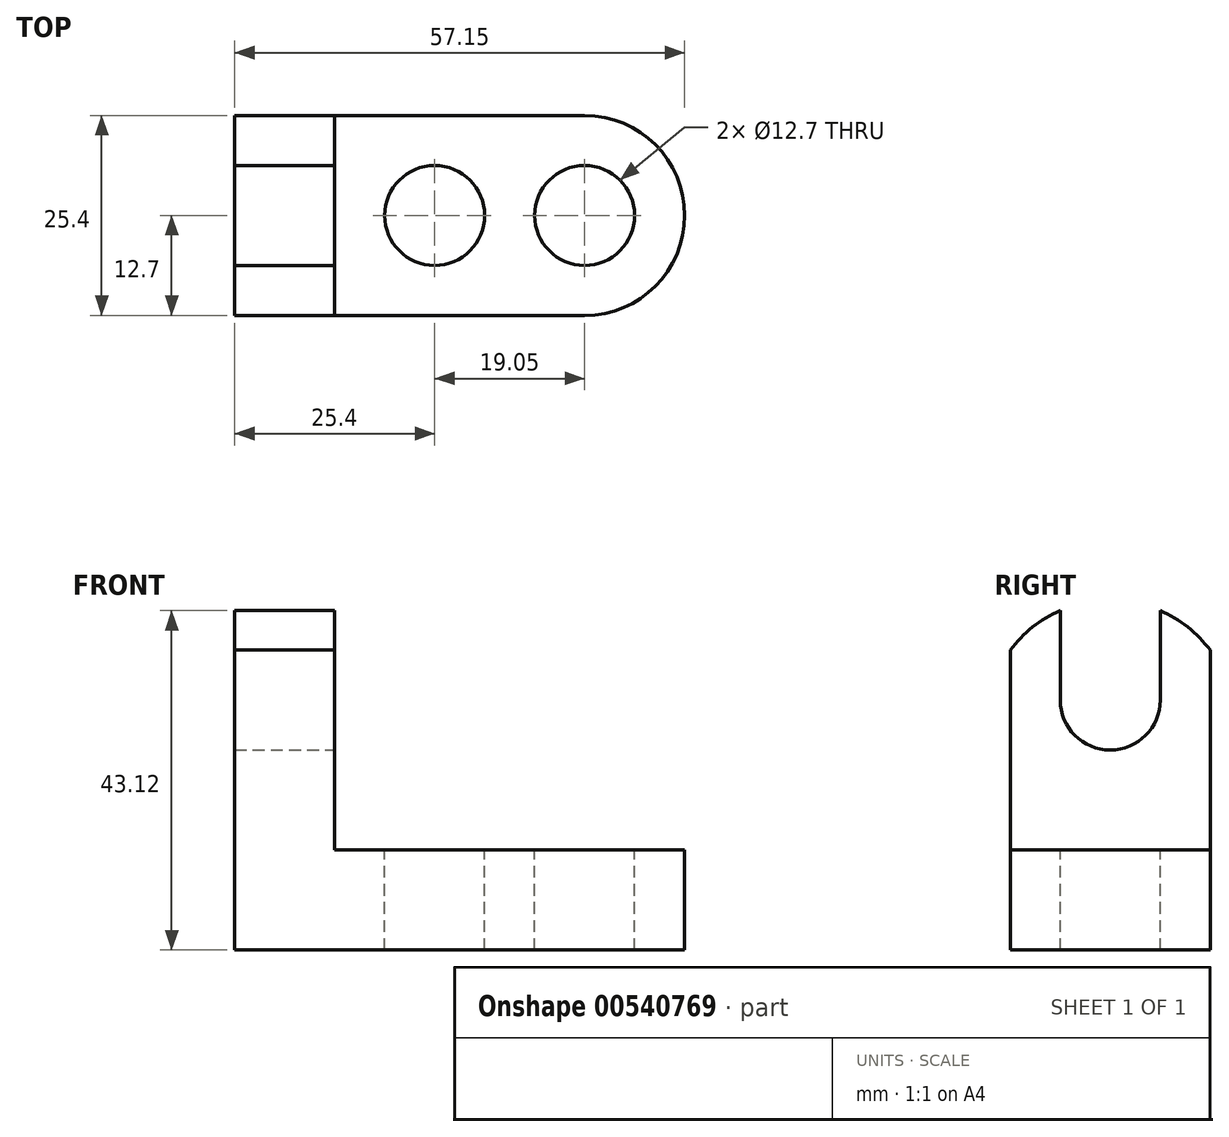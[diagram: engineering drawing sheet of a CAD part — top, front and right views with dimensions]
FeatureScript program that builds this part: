
annotation { "Feature Type Name" : "Feature", "Feature Type Description" : "" }
export const myFeature = defineFeature(function(context is Context, id is Id, definition is map)
    precondition{}
    {
        {
            var Q0;
            Q0=qCreatedBy(makeId("Front.planeOp"),FACE);
            var sketch = newSketch(context, id + "F0", { "sketchPlane" : qUnion([Q0])});
            skLineSegment(sketch, "E0", {"start": v(0, 0) * mm, "end": v(57.15, 0) * mm});
            skLineSegment(sketch, "E1", {"start": v(57.15, 0) * mm, "end": v(57.15, 12.7) * mm});
            skLineSegment(sketch, "E2", {"start": v(57.15, 12.7) * mm, "end": v(12.7, 12.7) * mm});
            skLineSegment(sketch, "E3", {"start": v(12.7, 12.7) * mm, "end": v(12.7, 44.45) * mm});
            skLineSegment(sketch, "E4", {"start": v(12.7, 44.45) * mm, "end": v(0, 44.45) * mm});
            skLineSegment(sketch, "E5", {"start": v(0, 44.45) * mm, "end": v(0, 0) * mm});
            skSolve(sketch);
        }
        {
            var Q0;
            Q0 = qSketchRegion(id + "F0", true);
            extrude(context, id + "F1", {"entities" : qUnion([Q0]), "depth" : 25.4 * mm, "offsetDistance" : 25.4 * mm});
        }
        {
            var Q0;
            Q0=makeQuery(id+"F1.opExtrude","SWEPT_FACE",FACE,{"disambiguationData":[OSD([sQuery(id+"F0.wireOp",EDGE,"E2")])]});
            var sketch = newSketch(context, id + "F2", { "sketchPlane" : qUnion([Q0])});
            skCircle(sketch, "E6", {"center": v(25.4, -12.7) * mm, "radius": 6.35 * mm});
            skCircle(sketch, "E7", {"center": v(44.45, -12.7) * mm, "radius": 6.35 * mm});
            skSolve(sketch);
        }
        {
            var Q0;
            Q0=makeQuery(id+"F2.imprint","IMPRINT",FACE,{"disambiguationData":[TD([[makeQuery(id+"F2.imprint","IMPRINT",EDGE,{"derivedFrom":sQuery(id+"F2.wireOp",EDGE,"E6")}),1.0]])]});
            var Q1;
            Q1=makeQuery(id+"F2.imprint","IMPRINT",FACE,{"disambiguationData":[TD([[makeQuery(id+"F2.imprint","IMPRINT",EDGE,{"derivedFrom":sQuery(id+"F2.wireOp",EDGE,"E7")}),1.0]])]});
            extrude(context, id + "F3", {"entities" : qUnion([Q0, Q1]), "operationType" : NewBodyOperationType.REMOVE, "oppositeDirection" : true, "depth" : 12.7 * mm, "offsetDistance" : 25.4 * mm});
        }
        {
            var Q0;
            Q0=makeQuery(id+"F1.opExtrude","SWEPT_FACE",FACE,{"disambiguationData":[OSD([sQuery(id+"F0.wireOp",EDGE,"E3")])]});
            var sketch = newSketch(context, id + "F4", { "sketchPlane" : qUnion([Q0])});
            skSolve(sketch);
        }
        {
            var Q0;
            Q0=makeQuery(id+"F1.opExtrude","SWEPT_FACE",FACE,{"disambiguationData":[OSD([sQuery(id+"F0.wireOp",EDGE,"E2")])]});
            var sketch = newSketch(context, id + "F5", { "sketchPlane" : qUnion([Q0])});
            skArc(sketch, "E8", {"start": v(44.45, -25.4) * mm, "mid": v(57.15, -12.7) * mm, "end": v(44.45, 0) * mm});
            skSolve(sketch);
        }
        {
            var Q0;
            {var subQ0=sQuery(id+"F5.wireOp",EDGE,"E8");var subQ1=sQuery(id+"F0.wireOp",EDGE,"E2");var subQ2=makeQuery(id+"F1.opExtrude","CAP_EDGE",EDGE,{"disambiguationData":[OSD([subQ1])],"isStart":true});var subQ3=makeQuery(id+"F5.imprint","INTERSECT",VERTEX,{"derivedFrom":[subQ2,subQ0]});Q0=makeQuery(id+"F5.imprint","IMPRINT",FACE,{"disambiguationData":[TD([[makeQuery(id+"F5.imprint","IMPRINT",EDGE,{"disambiguationData":[TD([[subQ3,1.0]])],"derivedFrom":subQ0}),-1.0]])]});}
            var Q1;
            {var subQ0=sQuery(id+"F5.wireOp",EDGE,"E8");var subQ1=sQuery(id+"F0.wireOp",EDGE,"E2");var subQ2=makeQuery(id+"F1.opExtrude","CAP_EDGE",EDGE,{"disambiguationData":[OSD([subQ1])],"isStart":false});var subQ3=makeQuery(id+"F5.imprint","INTERSECT",VERTEX,{"derivedFrom":[subQ2,subQ0]});Q1=makeQuery(id+"F5.imprint","IMPRINT",FACE,{"disambiguationData":[TD([[makeQuery(id+"F5.imprint","IMPRINT",EDGE,{"disambiguationData":[TD([[subQ3,-1.0]])],"derivedFrom":subQ0}),-1.0]])]});}
            extrude(context, id + "F6", {"entities" : qUnion([Q0, Q1]), "operationType" : NewBodyOperationType.REMOVE, "oppositeDirection" : true, "depth" : 12.7 * mm, "offsetDistance" : 25.4 * mm});
        }
        {
            var Q0;
            {var subQ0=sQuery(id+"F0.wireOp",EDGE,"E3");Q0=makeQuery(id+"F4.imprint","IMPRINT",FACE,{"disambiguationData":[TD([[makeQuery(id+"F4.imprint","IMPRINT",EDGE,{"derivedFrom":makeQuery(id+"F1.opExtrude","CAP_EDGE",EDGE,{"disambiguationData":[OSD([subQ0])],"isStart":true})}),1.0]])]});}
            var sketch = newSketch(context, id + "F7", { "sketchPlane" : qUnion([Q0])});
            skLineSegment(sketch, "E9.0", {"start": v(-25.4, 44.45) * mm, "end": v(0, 44.45) * mm});
            skCircle(sketch, "E10", {"center": v(-12.7, 31.75) * mm, "radius": 6.35 * mm});
            skLineSegment(sketch, "E11", {"start": v(-19.05, 31.75) * mm, "end": v(-19.05, 44.45) * mm});
            skLineSegment(sketch, "E12", {"start": v(-6.35, 31.75) * mm, "end": v(-6.35, 44.45) * mm});
            skSolve(sketch);
        }
        {
            var Q0;
            {var subQ0=sQuery(id+"F7.wireOp",EDGE,"E10");var subQ1=makeQuery(id+"F7.imprint","INTERSECT",VERTEX,{"derivedFrom":[subQ0,sQuery(id+"F7.wireOp",EDGE,"E11")]});Q0=makeQuery(id+"F7.imprint","IMPRINT",FACE,{"disambiguationData":[TD([[makeQuery(id+"F7.imprint","IMPRINT",EDGE,{"disambiguationData":[TD([[subQ1,1.0]])],"derivedFrom":subQ0}),1.0]])]});}
            var Q1;
            {var subQ0=sQuery(id+"F7.wireOp",EDGE,"E11");Q1=makeQuery(id+"F7.imprint","IMPRINT",FACE,{"disambiguationData":[TD([[makeQuery(id+"F7.imprint","IMPRINT",EDGE,{"derivedFrom":subQ0}),-1.0]])]});}
            extrude(context, id + "F8", {"entities" : qUnion([Q0, Q1]), "operationType" : NewBodyOperationType.REMOVE, "oppositeDirection" : true, "depth" : 12.7 * mm, "offsetDistance" : 25.4 * mm});
        }
        {
            var Q0;
            {var subQ0=sQuery(id+"F0.wireOp",EDGE,"E3");Q0=makeQuery(id+"F4.imprint","IMPRINT",FACE,{"disambiguationData":[TD([[makeQuery(id+"F4.imprint","IMPRINT",EDGE,{"derivedFrom":makeQuery(id+"F1.opExtrude","CAP_EDGE",EDGE,{"disambiguationData":[OSD([subQ0])],"isStart":true})}),1.0]])]});}
            var sketch = newSketch(context, id + "F9", { "sketchPlane" : qUnion([Q0])});
            skLineSegment(sketch, "E13.0", {"start": v(-25.4, 12.7) * mm, "end": v(-25.4, 44.45) * mm});
            skLineSegment(sketch, "E13.1", {"start": v(0, 44.45) * mm, "end": v(0, 0) * mm});
            skArc(sketch, "E14", {"start": v(0, 38.1) * mm, "mid": v(-12.7, 44.45) * mm, "end": v(-25.4, 38.1) * mm});
            skSolve(sketch);
        }
        {
            var Q0;
            {var subQ0=sQuery(id+"F9.wireOp",EDGE,"E13.0");var subQ3=sQuery(id+"F9.wireOp",EDGE,"E14");var subQ4=makeQuery(id+"F9.imprint","INTERSECT",VERTEX,{"derivedFrom":[subQ0,subQ3]});Q0=makeQuery(id+"F9.imprint","IMPRINT",FACE,{"disambiguationData":[TD([[makeQuery(id+"F9.imprint","IMPRINT",EDGE,{"disambiguationData":[TD([[subQ4,-1.0]])],"derivedFrom":subQ0}),-1.0]])]});}
            var Q1;
            {var subQ0=sQuery(id+"F9.wireOp",EDGE,"E13.1");var subQ3=sQuery(id+"F9.wireOp",EDGE,"E14");var subQ4=makeQuery(id+"F9.imprint","INTERSECT",VERTEX,{"derivedFrom":[subQ0,subQ3]});Q1=makeQuery(id+"F9.imprint","IMPRINT",FACE,{"disambiguationData":[TD([[makeQuery(id+"F9.imprint","IMPRINT",EDGE,{"disambiguationData":[TD([[subQ4,-1.0]])],"derivedFrom":subQ0}),1.0]])]});}
            extrude(context, id + "F10", {"entities" : qUnion([Q0, Q1]), "operationType" : NewBodyOperationType.REMOVE, "oppositeDirection" : true, "depth" : 25.4 * mm, "offsetDistance" : 25.4 * mm});
        }
    });
